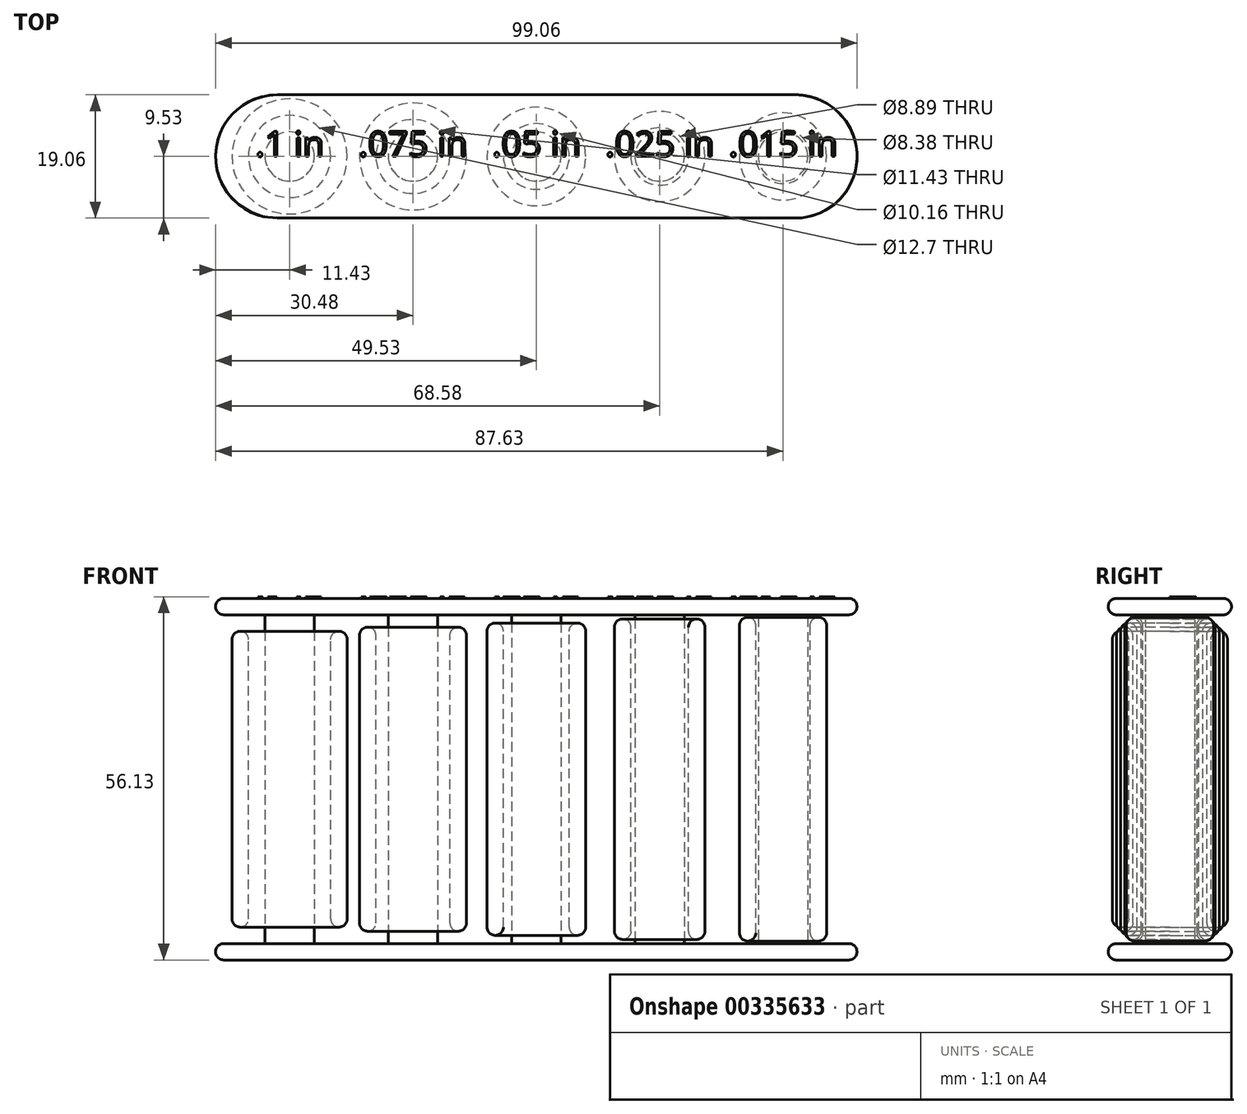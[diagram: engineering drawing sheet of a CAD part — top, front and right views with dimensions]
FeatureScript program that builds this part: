
annotation { "Feature Type Name" : "Feature", "Feature Type Description" : "" }
export const myFeature = defineFeature(function(context is Context, id is Id, definition is map)
    precondition{}
    {
        {
            var Q0;
            Q0=qCreatedBy(makeId("Top.planeOp"),FACE);
            var sketch = newSketch(context, id + "F0", { "sketchPlane" : qUnion([Q0])});
            skCircle(sketch, "E0", {"center": v(-38.1, 0) * mm, "radius": 3.81 * mm});
            skLineSegment(sketch, "E1", {"start": v(-40.27, 7.23) * mm, "end": v(86.73, 7.23) * mm, "construction": true});
            skLineSegment(sketch, "E2", {"start": v(-38.1, 0) * mm, "end": v(0, 0) * mm, "construction": true});
            skCircle(sketch, "E3.1.0.0", {"center": v(-19.05, 0) * mm, "radius": 3.81 * mm});
            skCircle(sketch, "E3.2.0.0", {"center": v(0, 0) * mm, "radius": 3.81 * mm});
            skCircle(sketch, "E3.3.0.0", {"center": v(19.05, 0) * mm, "radius": 3.81 * mm});
            skCircle(sketch, "E3.4.0.0", {"center": v(38.1, 0) * mm, "radius": 3.81 * mm});
            skLineSegment(sketch, "E3.direction1", {"start": v(-38.1, 0) * mm, "end": v(-19.05, 0) * mm, "construction": true});
            skSolve(sketch);
        }
        {
            var Q0;
            Q0=makeQuery(id+"F0.imprint","IMPRINT",FACE,{"disambiguationData":[TD([[makeQuery(id+"F0.imprint","IMPRINT",EDGE,{"derivedFrom":sQuery(id+"F0.wireOp",EDGE,"E0")}),1.0]])]});
            var Q1;
            Q1=makeQuery(id+"F0.imprint","IMPRINT",FACE,{"disambiguationData":[TD([[makeQuery(id+"F0.imprint","IMPRINT",EDGE,{"derivedFrom":sQuery(id+"F0.wireOp",EDGE,"E3.1.0.0")}),1.0]])]});
            var Q2;
            Q2=makeQuery(id+"F0.imprint","IMPRINT",FACE,{"disambiguationData":[TD([[makeQuery(id+"F0.imprint","IMPRINT",EDGE,{"derivedFrom":sQuery(id+"F0.wireOp",EDGE,"E3.2.0.0")}),1.0]])]});
            var Q3;
            Q3=makeQuery(id+"F0.imprint","IMPRINT",FACE,{"disambiguationData":[TD([[makeQuery(id+"F0.imprint","IMPRINT",EDGE,{"derivedFrom":sQuery(id+"F0.wireOp",EDGE,"E3.3.0.0")}),1.0]])]});
            var Q4;
            Q4=makeQuery(id+"F0.imprint","IMPRINT",FACE,{"disambiguationData":[TD([[makeQuery(id+"F0.imprint","IMPRINT",EDGE,{"derivedFrom":sQuery(id+"F0.wireOp",EDGE,"E3.4.0.0")}),1.0]])]});
            extrude(context, id + "F1", {"entities" : qUnion([Q0, Q1, Q2, Q3, Q4]), "endBound" : BoundingType.SYMMETRIC, "depth" : 50.8 * mm});
        }
        {
            var Q0;
            Q0=makeQuery(id+"F1.opExtrude","CAP_FACE",FACE,{"disambiguationData":[OSD([sQuery(id+"F0.wireOp",EDGE,"E0")])],"isStart":false});
            var sketch = newSketch(context, id + "F2", { "sketchPlane" : qUnion([Q0])});
            skLineSegment(sketch, "E4.bottom", {"start": v(40, 9.53) * mm, "end": v(-40, 9.53) * mm});
            skLineSegment(sketch, "E4.top", {"start": v(40, -9.53) * mm, "end": v(-40, -9.53) * mm});
            skLineSegment(sketch, "E4.left", {"start": v(49.53, 0) * mm, "end": v(49.53, 0) * mm});
            skLineSegment(sketch, "E4.right", {"start": v(-49.53, 0) * mm, "end": v(-49.53, 0) * mm});
            skPoint(sketch, "E4.middle", {"position": v(0, 0) * mm});
            skPoint(sketch, "E5.visualSharp", {"position": v(-49.53, 9.53) * mm});
            skArc(sketch, "E5.filletArc", {"start": v(-40, 9.53) * mm, "mid": v(-46.74, 6.74) * mm, "end": v(-49.53, 0) * mm});
            skPoint(sketch, "E6.visualSharp", {"position": v(-49.53, -9.53) * mm});
            skArc(sketch, "E6.filletArc", {"start": v(-49.53, 0) * mm, "mid": v(-46.74, -6.74) * mm, "end": v(-40, -9.53) * mm});
            skPoint(sketch, "E7.visualSharp", {"position": v(49.53, 9.53) * mm});
            skArc(sketch, "E7.filletArc", {"start": v(49.53, 0) * mm, "mid": v(46.74, 6.74) * mm, "end": v(40, 9.53) * mm});
            skPoint(sketch, "E8.visualSharp", {"position": v(49.53, -9.53) * mm});
            skArc(sketch, "E8.filletArc", {"start": v(40, -9.53) * mm, "mid": v(46.74, -6.74) * mm, "end": v(49.53, 0) * mm});
            skSolve(sketch);
        }
        {
            var Q0;
            Q0=makeQuery(id+"F2.imprint","IMPRINT",FACE,{"disambiguationData":[TD([[makeQuery(id+"F2.imprint","IMPRINT",EDGE,{"derivedFrom":sQuery(id+"F2.wireOp",EDGE,"E4.bottom")}),1.0]])]});
            var Q1;
            Q1=makeQuery(id+"F2.imprint","IMPRINT",FACE,{"disambiguationData":[TD([[makeQuery(id+"F2.imprint","IMPRINT",EDGE,{"derivedFrom":makeQuery(id+"F1.opExtrude","CAP_EDGE",EDGE,{"disambiguationData":[OSD([sQuery(id+"F0.wireOp",EDGE,"E0")])],"isStart":false})}),1.0]])]});
            extrude(context, id + "F3", {"entities" : qUnion([Q0, Q1]), "depth" : 2.54 * mm});
        }
        {
            var Q0;
            Q0=makeQuery(id+"F3.opExtrude","SWEPT_BODY",BODY,{"disambiguationData":[OSD([sQuery(id+"F2.wireOp",EDGE,"E4.bottom"),sQuery(id+"F2.wireOp",EDGE,"E4.top"),sQuery(id+"F2.wireOp",EDGE,"E5.filletArc"),sQuery(id+"F2.wireOp",EDGE,"E6.filletArc"),sQuery(id+"F2.wireOp",EDGE,"E7.filletArc"),sQuery(id+"F2.wireOp",EDGE,"E8.filletArc")])]});
            var Q1;
            Q1=qCreatedBy(makeId("Top.planeOp"),FACE);
            mirror(context, id + "F4", {"operationType" : NewBodyOperationType.ADD, "entities" : qUnion([Q0]), "mirrorPlane" : qUnion([Q1])});
        }
        {
            var Q0;
            Q0=qCreatedBy(makeId("Front.planeOp"),FACE);
            var sketch = newSketch(context, id + "F5", { "sketchPlane" : qUnion([Q0])});
            skLineSegment(sketch, "E9", {"start": v(-35.9, 0) * mm, "end": v(32.63, 0) * mm, "construction": true});
            skLineSegment(sketch, "E10.bottom", {"start": v(-47, 22.86) * mm, "end": v(-44.45, 22.86) * mm});
            skLineSegment(sketch, "E10.top", {"start": v(-47, -22.86) * mm, "end": v(-44.45, -22.86) * mm});
            skLineSegment(sketch, "E10.left", {"start": v(-47, 22.86) * mm, "end": v(-47, -22.86) * mm});
            skLineSegment(sketch, "E10.right", {"start": v(-44.45, 22.86) * mm, "end": v(-44.45, -22.86) * mm});
            skPoint(sketch, "E10.middle", {"position": v(-45.72, 0) * mm});
            skLineSegment(sketch, "E11.bottom", {"start": v(-27.3, 23.5) * mm, "end": v(-24.77, 23.5) * mm});
            skLineSegment(sketch, "E11.top", {"start": v(-27.3, -23.5) * mm, "end": v(-24.77, -23.5) * mm});
            skLineSegment(sketch, "E11.left", {"start": v(-27.3, 23.5) * mm, "end": v(-27.3, -23.5) * mm});
            skLineSegment(sketch, "E11.right", {"start": v(-24.77, 23.5) * mm, "end": v(-24.77, -23.5) * mm});
            skPoint(sketch, "E11.middle", {"position": v(-26.04, 0) * mm});
            skLineSegment(sketch, "E12.bottom", {"start": v(-7.62, 24.13) * mm, "end": v(-5.08, 24.13) * mm});
            skLineSegment(sketch, "E12.top", {"start": v(-7.62, -24.13) * mm, "end": v(-5.08, -24.13) * mm});
            skLineSegment(sketch, "E12.left", {"start": v(-7.62, 24.13) * mm, "end": v(-7.62, -24.13) * mm});
            skLineSegment(sketch, "E12.right", {"start": v(-5.08, 24.13) * mm, "end": v(-5.08, -24.13) * mm});
            skPoint(sketch, "E12.middle", {"position": v(-6.35, 0) * mm});
            skLineSegment(sketch, "E13.bottom", {"start": v(14.6, 24.77) * mm, "end": v(12.06, 24.77) * mm});
            skLineSegment(sketch, "E13.top", {"start": v(14.6, -24.77) * mm, "end": v(12.06, -24.77) * mm});
            skLineSegment(sketch, "E13.left", {"start": v(14.6, 24.77) * mm, "end": v(14.6, -24.77) * mm});
            skLineSegment(sketch, "E13.right", {"start": v(12.06, 24.77) * mm, "end": v(12.06, -24.77) * mm});
            skPoint(sketch, "E13.middle", {"position": v(13.33, 0) * mm});
            skLineSegment(sketch, "E14.bottom", {"start": v(31.37, 25.02) * mm, "end": v(33.9, 25.02) * mm});
            skLineSegment(sketch, "E14.top", {"start": v(31.37, -25.02) * mm, "end": v(33.9, -25.02) * mm});
            skLineSegment(sketch, "E14.left", {"start": v(31.37, 25.02) * mm, "end": v(31.37, -25.02) * mm});
            skLineSegment(sketch, "E14.right", {"start": v(33.9, 25.02) * mm, "end": v(33.9, -25.02) * mm});
            skPoint(sketch, "E14.middle", {"position": v(32.64, 0) * mm});
            skLineSegment(sketch, "E15", {"start": v(-41.91, -25.4) * mm, "end": v(-41.91, 25.4) * mm});
            skLineSegment(sketch, "E16", {"start": v(-34.3, 25.4) * mm, "end": v(-34.3, -25.4) * mm});
            skLineSegment(sketch, "E17", {"start": v(-22.86, -25.4) * mm, "end": v(-22.86, 25.4) * mm});
            skLineSegment(sketch, "E18", {"start": v(-15.24, 25.4) * mm, "end": v(-15.24, -25.4) * mm});
            skLineSegment(sketch, "E19", {"start": v(-3.81, -25.4) * mm, "end": v(-3.81, 25.4) * mm});
            skLineSegment(sketch, "E20", {"start": v(3.81, 25.4) * mm, "end": v(3.81, -25.4) * mm});
            skLineSegment(sketch, "E21", {"start": v(15.24, -25.4) * mm, "end": v(15.24, 25.4) * mm});
            skLineSegment(sketch, "E22", {"start": v(22.86, 25.4) * mm, "end": v(22.86, -25.4) * mm});
            skLineSegment(sketch, "E23", {"start": v(34.29, -25.4) * mm, "end": v(34.29, 25.4) * mm});
            skLineSegment(sketch, "E24", {"start": v(41.9, 25.4) * mm, "end": v(41.9, -25.4) * mm});
            skLineSegment(sketch, "E25", {"start": v(-49.53, 25.4) * mm, "end": v(-49.53, 27.94) * mm});
            skLineSegment(sketch, "E26.0.0", {"start": v(-40, 25.4) * mm, "end": v(40, 25.4) * mm});
            skLineSegment(sketch, "E26.0.1", {"start": v(40, 25.4) * mm, "end": v(40, 27.94) * mm});
            skLineSegment(sketch, "E26.0.2", {"start": v(40, 27.94) * mm, "end": v(-40, 27.94) * mm});
            skLineSegment(sketch, "E26.0.3", {"start": v(-40, 27.94) * mm, "end": v(-40, 25.4) * mm});
            skLineSegment(sketch, "E27", {"start": v(-41.91, 25.4) * mm, "end": v(-34.3, 25.4) * mm});
            skLineSegment(sketch, "E28", {"start": v(-22.86, 25.4) * mm, "end": v(-15.24, 25.4) * mm});
            skLineSegment(sketch, "E29", {"start": v(-3.81, 25.4) * mm, "end": v(3.81, 25.4) * mm});
            skLineSegment(sketch, "E30", {"start": v(15.24, 25.4) * mm, "end": v(22.86, 25.4) * mm});
            skLineSegment(sketch, "E31", {"start": v(34.29, 25.4) * mm, "end": v(41.9, 25.4) * mm});
            skLineSegment(sketch, "E32", {"start": v(-38.1, 25.4) * mm, "end": v(-38.1, -4.69) * mm});
            skLineSegment(sketch, "E33", {"start": v(-19.05, 25.4) * mm, "end": v(-19.05, -4.53) * mm});
            skLineSegment(sketch, "E34", {"start": v(0, 25.4) * mm, "end": v(0, -7.56) * mm});
            skLineSegment(sketch, "E35", {"start": v(19.05, 25.4) * mm, "end": v(19.05, -2.67) * mm});
            skLineSegment(sketch, "E36", {"start": v(38.1, 25.4) * mm, "end": v(38.1, -4.3) * mm});
            skSolve(sketch);
        }
        {
            var Q0;
            Q0=makeQuery(id+"F5.imprint","IMPRINT",FACE,{"disambiguationData":[TD([[makeQuery(id+"F5.imprint","IMPRINT",EDGE,{"derivedFrom":sQuery(id+"F5.wireOp",EDGE,"E10.bottom")}),-1.0]])]});
            var Q1;
            Q1=sQuery(id+"F5.wireOp",EDGE,"E32");
            revolve(context, id + "F6", {"entities" : qUnion([Q0]), "axis" : qUnion([Q1]), "revolveType" : RevolveType.FULL});
        }
        {
            var Q0;
            Q0=makeQuery(id+"F5.imprint","IMPRINT",FACE,{"disambiguationData":[TD([[makeQuery(id+"F5.imprint","IMPRINT",EDGE,{"derivedFrom":sQuery(id+"F5.wireOp",EDGE,"E11.bottom")}),-1.0]])]});
            var Q1;
            Q1=sQuery(id+"F5.wireOp",EDGE,"E33");
            revolve(context, id + "F7", {"entities" : qUnion([Q0]), "axis" : qUnion([Q1]), "revolveType" : RevolveType.FULL});
        }
        {
            var Q0;
            Q0=makeQuery(id+"F5.imprint","IMPRINT",FACE,{"disambiguationData":[TD([[makeQuery(id+"F5.imprint","IMPRINT",EDGE,{"derivedFrom":sQuery(id+"F5.wireOp",EDGE,"E12.bottom")}),-1.0]])]});
            var Q1;
            Q1=sQuery(id+"F5.wireOp",EDGE,"E34");
            revolve(context, id + "F8", {"entities" : qUnion([Q0]), "axis" : qUnion([Q1]), "revolveType" : RevolveType.FULL});
        }
        {
            var Q0;
            Q0=makeQuery(id+"F5.imprint","IMPRINT",FACE,{"disambiguationData":[TD([[makeQuery(id+"F5.imprint","IMPRINT",EDGE,{"derivedFrom":sQuery(id+"F5.wireOp",EDGE,"E13.bottom")}),1.0]])]});
            var Q1;
            Q1=sQuery(id+"F5.wireOp",EDGE,"E35");
            revolve(context, id + "F9", {"entities" : qUnion([Q0]), "axis" : qUnion([Q1]), "revolveType" : RevolveType.FULL});
        }
        {
            var Q0;
            Q0=makeQuery(id+"F5.imprint","IMPRINT",FACE,{"disambiguationData":[TD([[makeQuery(id+"F5.imprint","IMPRINT",EDGE,{"derivedFrom":sQuery(id+"F5.wireOp",EDGE,"E14.bottom")}),-1.0]])]});
            var Q1;
            Q1=sQuery(id+"F5.wireOp",EDGE,"E36");
            revolve(context, id + "F10", {"entities" : qUnion([Q0]), "axis" : qUnion([Q1]), "revolveType" : RevolveType.FULL});
        }
        {
            var Q0;
            Q0=makeQuery(id+"F6.opRevolve","SWEPT_FACE",FACE,{"disambiguationData":[OSD([sQuery(id+"F5.wireOp",EDGE,"E10.bottom")])]});
            var Q1;
            Q1=makeQuery(id+"F7.opRevolve","SWEPT_FACE",FACE,{"disambiguationData":[OSD([sQuery(id+"F5.wireOp",EDGE,"E11.bottom")])]});
            var Q2;
            Q2=makeQuery(id+"F8.opRevolve","SWEPT_FACE",FACE,{"disambiguationData":[OSD([sQuery(id+"F5.wireOp",EDGE,"E12.bottom")])]});
            var Q3;
            Q3=makeQuery(id+"F9.opRevolve","SWEPT_FACE",FACE,{"disambiguationData":[OSD([sQuery(id+"F5.wireOp",EDGE,"E13.bottom")])]});
            var Q4;
            Q4=makeQuery(id+"F10.opRevolve","SWEPT_FACE",FACE,{"disambiguationData":[OSD([sQuery(id+"F5.wireOp",EDGE,"E14.bottom")])]});
            var Q5;
            Q5=makeQuery(id+"F10.opRevolve","SWEPT_FACE",FACE,{"disambiguationData":[OSD([sQuery(id+"F5.wireOp",EDGE,"E14.top")])]});
            var Q6;
            Q6=makeQuery(id+"F9.opRevolve","SWEPT_FACE",FACE,{"disambiguationData":[OSD([sQuery(id+"F5.wireOp",EDGE,"E13.top")])]});
            var Q7;
            Q7=makeQuery(id+"F8.opRevolve","SWEPT_FACE",FACE,{"disambiguationData":[OSD([sQuery(id+"F5.wireOp",EDGE,"E12.top")])]});
            var Q8;
            Q8=makeQuery(id+"F7.opRevolve","SWEPT_FACE",FACE,{"disambiguationData":[OSD([sQuery(id+"F5.wireOp",EDGE,"E11.top")])]});
            var Q9;
            Q9=makeQuery(id+"F6.opRevolve","SWEPT_FACE",FACE,{"disambiguationData":[OSD([sQuery(id+"F5.wireOp",EDGE,"E10.top")])]});
            var Q10;
            Q10=makeQuery(id+"F4.opPattern","COPY",FACE,{"derivedFrom":makeQuery(id+"F3.opExtrude","SWEPT_FACE",FACE,{"disambiguationData":[OSD([sQuery(id+"F2.wireOp",EDGE,"E5.filletArc"),sQuery(id+"F2.wireOp",EDGE,"E6.filletArc")])]}),"instanceName":"1"});
            var Q11;
            Q11=makeQuery(id+"F3.opExtrude","SWEPT_FACE",FACE,{"disambiguationData":[OSD([sQuery(id+"F2.wireOp",EDGE,"E4.top")])]});
            fillet(context, id + "F11", {"entities" : qUnion([Q0, Q1, Q2, Q3, Q4, Q5, Q6, Q7, Q8, Q9, Q10, Q11]), "radius" : 1.27 * mm, "tangentPropagation" : true, "allowEdgeOverflow" : false});
        }
        {
            var Q0;
            Q0=makeQuery(id+"F3.opExtrude","CAP_FACE",FACE,{"disambiguationData":[OSD([sQuery(id+"F2.wireOp",EDGE,"E4.bottom"),sQuery(id+"F2.wireOp",EDGE,"E4.top"),sQuery(id+"F2.wireOp",EDGE,"E5.filletArc"),sQuery(id+"F2.wireOp",EDGE,"E6.filletArc"),sQuery(id+"F2.wireOp",EDGE,"E7.filletArc"),sQuery(id+"F2.wireOp",EDGE,"E8.filletArc")])],"isStart":false});
            var sketch = newSketch(context, id + "F12", { "sketchPlane" : qUnion([Q0])});
            skText(sketch, "E37", { "text": ".1 in", "fontName": "OpenSans-Regular.ttf"});
            skText(sketch, "E38", { "text": ".075 in", "fontName": "OpenSans-Regular.ttf"});
            skText(sketch, "E39", { "text": ".05 in", "fontName": "OpenSans-Regular.ttf"});
            skText(sketch, "E40", { "text": ".015 in", "fontName": "OpenSans-Regular.ttf"});
            skText(sketch, "E41", { "text": ".025 in", "fontName": "OpenSans-Regular.ttf"});
            const initialGuessF12  = {"E37": [-0.04338, 0, 1, 0, 0.0039], "E38": [-0.02743, 0, 1, 0, 0.0039], "E39": [-0.00683, 0, 1, 0, 0.0039], "E40": [0.02972, 0, 1, 0, 0.0039], "E41": [0.01067, 0, 1, 0, 0.0039]};
            skSetInitialGuess(sketch, initialGuessF12);
            skSolve(sketch);
        }
        {
            var Q0;
            Q0 = qSketchRegion(id + "F12", true);
            extrude(context, id + "F13", {"entities" : qUnion([Q0]), "operationType" : NewBodyOperationType.ADD, "depth" : 0.25 * mm});
        }
    });
